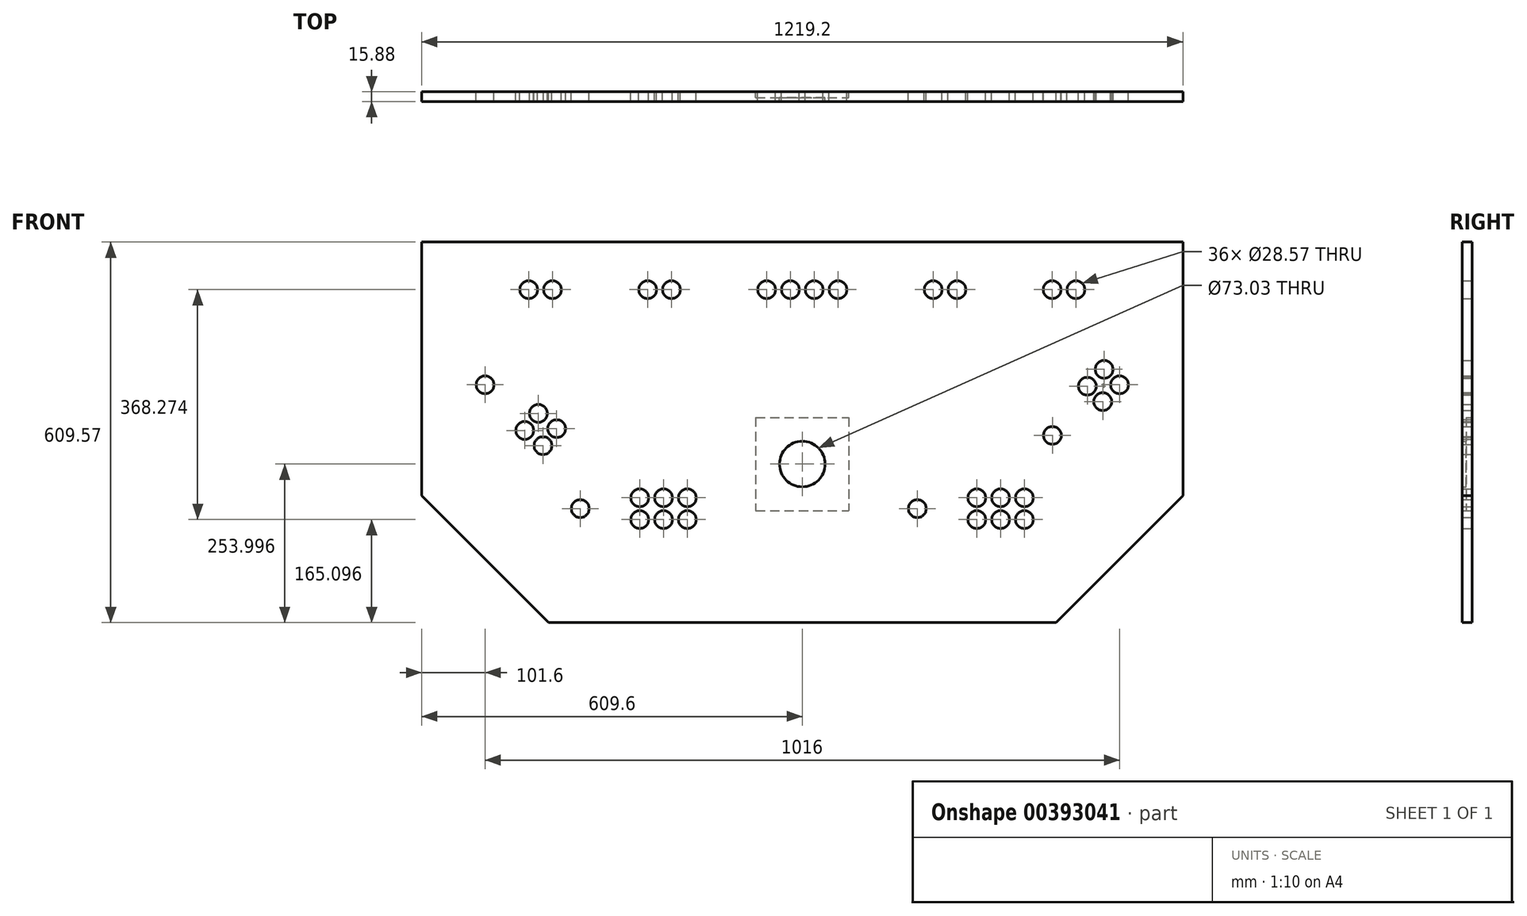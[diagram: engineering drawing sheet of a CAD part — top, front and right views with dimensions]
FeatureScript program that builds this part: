
annotation { "Feature Type Name" : "Feature", "Feature Type Description" : "" }
export const myFeature = defineFeature(function(context is Context, id is Id, definition is map)
    precondition{}
    {
        {
            var Q0;
            Q0=qCreatedBy(makeId("Front.planeOp"),FACE);
            var sketch = newSketch(context, id + "F0", { "sketchPlane" : qUnion([Q0])});
            skLineSegment(sketch, "E0", {"start": v(-609.6, 0) * mm, "end": v(609.6, 0) * mm});
            skLineSegment(sketch, "E1", {"start": v(609.6, -406.4) * mm, "end": v(609.6, 0) * mm});
            skLineSegment(sketch, "E2", {"start": v(609.6, -406.4) * mm, "end": v(406.4, -609.57) * mm});
            skLineSegment(sketch, "E3", {"start": v(406.4, -609.57) * mm, "end": v(-406.4, -609.57) * mm});
            skLineSegment(sketch, "E4", {"start": v(-406.4, -609.57) * mm, "end": v(-609.6, -406.4) * mm});
            skLineSegment(sketch, "E5", {"start": v(-609.6, -406.4) * mm, "end": v(-609.6, 0) * mm});
            skLineSegment(sketch, "E6", {"start": v(0, 35.87) * mm, "end": v(0, -746.64) * mm, "construction": true});
            skLineSegment(sketch, "E7.bottom", {"start": v(-74.61, -280.96) * mm, "end": v(74.61, -280.96) * mm});
            skLineSegment(sketch, "E7.top", {"start": v(-74.61, -430.19) * mm, "end": v(74.61, -430.19) * mm});
            skLineSegment(sketch, "E7.left", {"start": v(-74.61, -280.96) * mm, "end": v(-74.61, -430.19) * mm});
            skLineSegment(sketch, "E7.right", {"start": v(74.61, -280.96) * mm, "end": v(74.61, -430.19) * mm});
            skLineSegment(sketch, "E8", {"start": v(-74.61, -280.96) * mm, "end": v(74.61, -430.19) * mm, "construction": true});
            skCircle(sketch, "E9", {"center": v(0, -355.57) * mm, "radius": 36.51 * mm});
            skCircle(sketch, "E10", {"center": v(-222.25, -409.55) * mm, "radius": 14.29 * mm});
            skCircle(sketch, "E11", {"center": v(-184.15, -409.55) * mm, "radius": 14.29 * mm});
            skCircle(sketch, "E12", {"center": v(-260.35, -409.55) * mm, "radius": 14.29 * mm});
            skCircle(sketch, "E13", {"center": v(-260.35, -444.47) * mm, "radius": 14.29 * mm});
            skCircle(sketch, "E14", {"center": v(-222.25, -444.47) * mm, "radius": 14.29 * mm});
            skCircle(sketch, "E15", {"center": v(-184.15, -444.47) * mm, "radius": 14.29 * mm});
            skCircle(sketch, "E16", {"center": v(-355.6, -427.01) * mm, "radius": 14.29 * mm});
            skCircle(sketch, "E17", {"center": v(317.5, -409.55) * mm, "radius": 14.29 * mm});
            skCircle(sketch, "E18", {"center": v(355.6, -409.55) * mm, "radius": 14.29 * mm});
            skCircle(sketch, "E19", {"center": v(279.4, -409.55) * mm, "radius": 14.29 * mm});
            skCircle(sketch, "E20", {"center": v(279.4, -444.47) * mm, "radius": 14.29 * mm});
            skCircle(sketch, "E21", {"center": v(317.5, -444.47) * mm, "radius": 14.29 * mm});
            skCircle(sketch, "E22", {"center": v(355.6, -444.47) * mm, "radius": 14.29 * mm});
            skCircle(sketch, "E23", {"center": v(184.15, -427.01) * mm, "radius": 14.29 * mm});
            skCircle(sketch, "E24", {"center": v(-415.24, -326.12) * mm, "radius": 14.29 * mm});
            skCircle(sketch, "E25", {"center": v(-393.44, -298.83) * mm, "radius": 14.29 * mm});
            skCircle(sketch, "E26", {"center": v(-422.7, -274.43) * mm, "radius": 14.29 * mm});
            skCircle(sketch, "E27", {"center": v(-444.5, -301.71) * mm, "radius": 14.29 * mm});
            skCircle(sketch, "E28", {"center": v(-508, -228.6) * mm, "radius": 14.29 * mm});
            skCircle(sketch, "E29", {"center": v(247.65, -76.2) * mm, "radius": 14.29 * mm});
            skCircle(sketch, "E30", {"center": v(209.55, -76.2) * mm, "radius": 14.29 * mm});
            skCircle(sketch, "E31", {"center": v(438.15, -76.2) * mm, "radius": 14.29 * mm});
            skCircle(sketch, "E32", {"center": v(400.05, -76.2) * mm, "radius": 14.29 * mm});
            skPoint(sketch, "E33.endSnap0", {"position": v(609.6, -203.2) * mm});
            skCircle(sketch, "E34", {"center": v(-19.05, -76.2) * mm, "radius": 14.29 * mm});
            skCircle(sketch, "E35", {"center": v(-57.15, -76.2) * mm, "radius": 14.29 * mm});
            skCircle(sketch, "E36.MirrorC", {"center": v(19.05, -76.2) * mm, "radius": 14.29 * mm});
            skCircle(sketch, "E37.MirrorC", {"center": v(57.15, -76.2) * mm, "radius": 14.29 * mm});
            skCircle(sketch, "E38.MirrorC", {"center": v(-209.55, -76.2) * mm, "radius": 14.29 * mm});
            skCircle(sketch, "E39.MirrorC", {"center": v(-247.65, -76.2) * mm, "radius": 14.29 * mm});
            skCircle(sketch, "E40.MirrorC", {"center": v(-400.05, -76.2) * mm, "radius": 14.29 * mm});
            skCircle(sketch, "E41.MirrorC", {"center": v(-438.15, -76.2) * mm, "radius": 14.29 * mm});
            skLineSegment(sketch, "E42", {"start": v(-422.7, -274.43) * mm, "end": v(-444.5, -301.71) * mm, "construction": true});
            skLineSegment(sketch, "E43", {"start": v(-508, -228.6) * mm, "end": v(-433.6, -288.07) * mm, "construction": true});
            skCircle(sketch, "E44.MirrorC", {"center": v(456.42, -230.9) * mm, "radius": 14.29 * mm});
            skCircle(sketch, "E45.MirrorC", {"center": v(481.11, -255.6) * mm, "radius": 14.29 * mm});
            skCircle(sketch, "E46.MirrorC", {"center": v(508, -228.6) * mm, "radius": 14.29 * mm});
            skCircle(sketch, "E47.MirrorC", {"center": v(483.3, -203.9) * mm, "radius": 14.29 * mm});
            skLineSegment(sketch, "E48", {"start": v(400.47, -309.66) * mm, "end": v(467.83, -242.3) * mm, "construction": true});
            skLineSegment(sketch, "E49", {"start": v(456.42, -230.9) * mm, "end": v(481.11, -255.6) * mm, "construction": true});
            skCircle(sketch, "E50.MirrorC", {"center": v(400.47, -309.66) * mm, "radius": 14.29 * mm});
            skSolve(sketch);
        }
        {
            var Q0;
            Q0=makeQuery(id+"F0.imprint","IMPRINT",FACE,{"disambiguationData":[TD([[makeQuery(id+"F0.imprint","IMPRINT",EDGE,{"derivedFrom":sQuery(id+"F0.wireOp",EDGE,"E0")}),-1.0]])]});
            extrude(context, id + "F1", {"entities" : qUnion([Q0]), "depth" : 15.88 * mm});
        }
        {
            var Q0;
            Q0=makeQuery(id+"F0.imprint","IMPRINT",FACE,{"disambiguationData":[TD([[makeQuery(id+"F0.imprint","IMPRINT",EDGE,{"derivedFrom":sQuery(id+"F0.wireOp",EDGE,"E7.bottom")}),-1.0]])]});
            extrude(context, id + "F2", {"entities" : qUnion([Q0]), "operationType" : NewBodyOperationType.ADD, "depth" : 15.88 * mm, "hasSecondDirection" : true, "secondDirectionOppositeDirection" : false, "secondDirectionDepth" : 9.52 * mm});
        }
    });
